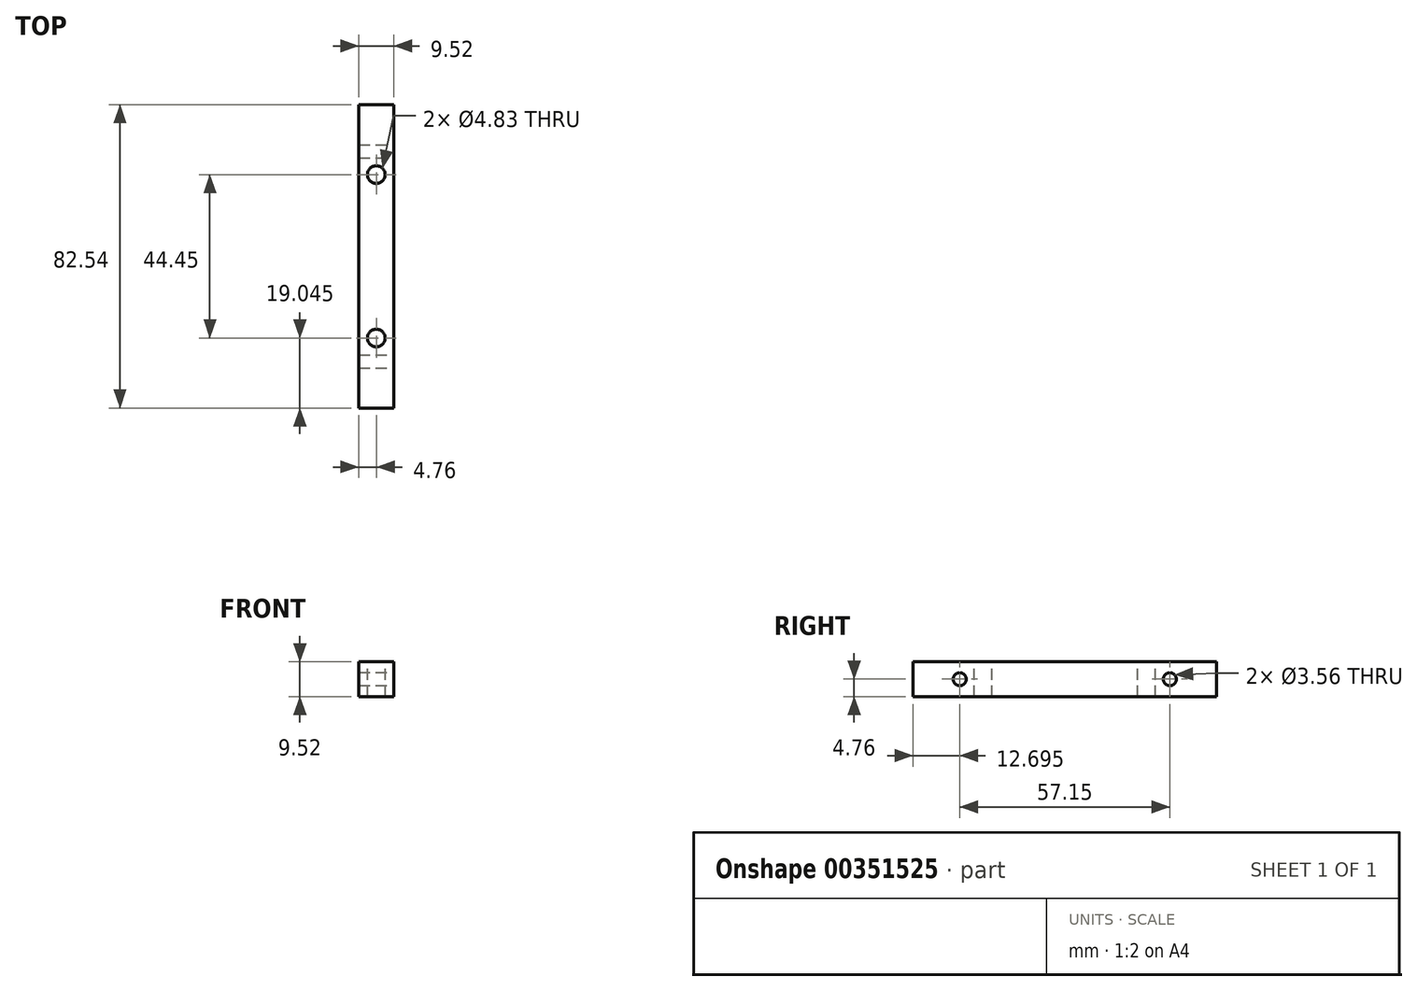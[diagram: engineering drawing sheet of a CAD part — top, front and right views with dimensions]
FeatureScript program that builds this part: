
annotation { "Feature Type Name" : "Feature", "Feature Type Description" : "" }
export const myFeature = defineFeature(function(context is Context, id is Id, definition is map)
    precondition{}
    {
        {
            var Q0;
            Q0=qCreatedBy(makeId("Front.planeOp"),FACE);
            var sketch = newSketch(context, id + "F0", { "sketchPlane" : qUnion([Q0])});
            skLineSegment(sketch, "E0.bottom", {"start": v(4.76, 4.76) * mm, "end": v(-4.76, 4.76) * mm});
            skLineSegment(sketch, "E0.top", {"start": v(4.76, -4.76) * mm, "end": v(-4.76, -4.76) * mm});
            skLineSegment(sketch, "E0.left", {"start": v(4.76, 4.76) * mm, "end": v(4.76, -4.76) * mm});
            skLineSegment(sketch, "E0.right", {"start": v(-4.76, 4.76) * mm, "end": v(-4.76, -4.76) * mm});
            skPoint(sketch, "E0.middle", {"position": v(0, 0) * mm});
            skSolve(sketch);
        }
        {
            var Q0;
            Q0 = qSketchRegion(id + "F0", true);
            extrude(context, id + "F1", {"entities" : qUnion([Q0]), "depth" : 82.55 * mm, "symmetric" : true});
        }
        {
            var Q0;
            Q0=makeQuery(id+"F1.opExtrude","SWEPT_FACE",FACE,{"disambiguationData":[OSD([sQuery(id+"F0.wireOp",EDGE,"E0.left")])]});
            var sketch = newSketch(context, id + "F2", { "sketchPlane" : qUnion([Q0])});
            skCircle(sketch, "E1", {"center": v(-28.58, 0) * mm, "radius": 1.78 * mm});
            skCircle(sketch, "E2", {"center": v(28.58, 0) * mm, "radius": 1.78 * mm});
            skSolve(sketch);
        }
        {
            var Q0;
            Q0 = qSketchRegion(id + "F2", true);
            var Q1;
            Q1=makeQuery(id+"F1.opExtrude","SWEPT_FACE",FACE,{"disambiguationData":[OSD([sQuery(id+"F0.wireOp",EDGE,"E0.right")])]});
            extrude(context, id + "F3", {"entities" : qUnion([Q0]), "operationType" : NewBodyOperationType.REMOVE, "endBound" : BoundingType.UP_TO_SURFACE, "oppositeDirection" : true, "endBoundEntityFace" : qUnion([Q1]), "depth" : 25.4 * mm});
        }
        {
            var Q0;
            Q0=makeQuery(id+"F1.opExtrude","SWEPT_FACE",FACE,{"disambiguationData":[OSD([sQuery(id+"F0.wireOp",EDGE,"E0.bottom")])]});
            var sketch = newSketch(context, id + "F4", { "sketchPlane" : qUnion([Q0])});
            skCircle(sketch, "E3", {"center": v(0, -22.23) * mm, "radius": 2.41 * mm});
            skCircle(sketch, "E4", {"center": v(0, 22.23) * mm, "radius": 2.41 * mm});
            skSolve(sketch);
        }
        {
            var Q0;
            Q0 = qSketchRegion(id + "F4", true);
            var Q1;
            Q1=makeQuery(id+"F1.opExtrude","SWEPT_FACE",FACE,{"disambiguationData":[OSD([sQuery(id+"F0.wireOp",EDGE,"E0.top")])]});
            extrude(context, id + "F5", {"entities" : qUnion([Q0]), "operationType" : NewBodyOperationType.REMOVE, "endBound" : BoundingType.UP_TO_SURFACE, "oppositeDirection" : true, "endBoundEntityFace" : qUnion([Q1]), "depth" : 25.4 * mm});
        }
    });
